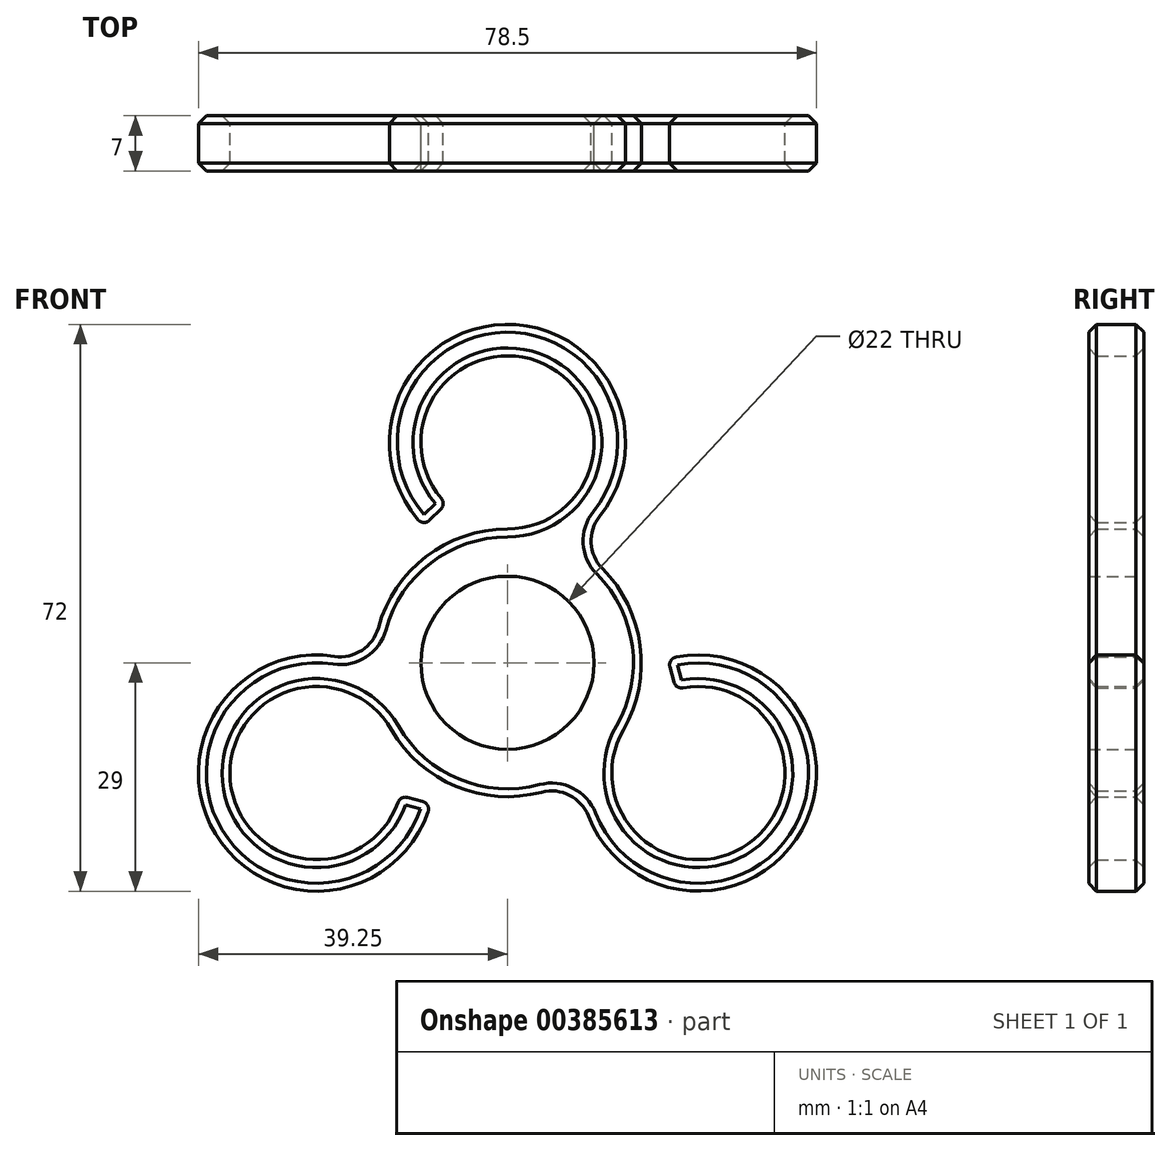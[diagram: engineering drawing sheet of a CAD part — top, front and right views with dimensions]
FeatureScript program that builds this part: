
annotation { "Feature Type Name" : "Feature", "Feature Type Description" : "" }
export const myFeature = defineFeature(function(context is Context, id is Id, definition is map)
    precondition{}
    {
        {
            var Q0;
            Q0=qCreatedBy(makeId("Front.planeOp"),FACE);
            var sketch = newSketch(context, id + "F0", { "sketchPlane" : qUnion([Q0])});
            skCircle(sketch, "E0", {"center": v(0, 0) * mm, "radius": 11 * mm});
            skArc(sketch, "E1", {"start": v(0, 17) * mm, "mid": v(-10.32, 13.5) * mm, "end": v(-16.4, 4.46) * mm});
            skArc(sketch, "E2", {"start": v(0, 17) * mm, "mid": v(4.63, 37.98) * mm, "end": v(-8.4, 20.9) * mm});
            skLineSegment(sketch, "E3", {"start": v(-8.46, 19.54) * mm, "end": v(-9.87, 18.13) * mm});
            skArc(sketch, "E4", {"start": v(11.7, 18.63) * mm, "mid": v(-0.3, 43) * mm, "end": v(-11.34, 18.18) * mm});
            skPoint(sketch, "E5.visualSharp", {"position": v(-7.78, 20.22) * mm});
            skArc(sketch, "E5.filletArc", {"start": v(-8.46, 19.54) * mm, "mid": v(-8.16, 20.2) * mm, "end": v(-8.4, 20.9) * mm});
            skPoint(sketch, "E6.visualSharp", {"position": v(-10.6, 17.4) * mm});
            skArc(sketch, "E6.filletArc", {"start": v(-11.34, 18.18) * mm, "mid": v(-10.62, 17.83) * mm, "end": v(-9.87, 18.13) * mm});
            skPoint(sketch, "E7.visualSharp", {"position": v(7.73, 15.14) * mm});
            skArc(sketch, "E7.filletArc", {"start": v(11.7, 18.63) * mm, "mid": v(10.62, 15.23) * mm, "end": v(12.06, 11.98) * mm});
            skPoint(sketch, "E8.1.0", {"position": v(-13.62, -16.85) * mm});
            skArc(sketch, "E8.1.1", {"start": v(-21.98, 0.83) * mm, "mid": v(-18.5, 1.58) * mm, "end": v(-16.4, 4.46) * mm});
            skArc(sketch, "E8.1.2", {"start": v(-21.98, 0.83) * mm, "mid": v(-37.1, -21.75) * mm, "end": v(-10.07, -18.9) * mm});
            skArc(sketch, "E8.1.3", {"start": v(-14.72, -8.5) * mm, "mid": v(-35.2, -14.98) * mm, "end": v(-13.9, -17.72) * mm});
            skPoint(sketch, "E8.1.4", {"position": v(-9.76, -17.88) * mm});
            skPoint(sketch, "E8.1.5", {"position": v(-16.98, -0.88) * mm});
            skLineSegment(sketch, "E8.1.6", {"start": v(-12.7, -17.1) * mm, "end": v(-10.76, -17.61) * mm});
            skArc(sketch, "E8.1.7", {"start": v(-10.07, -18.9) * mm, "mid": v(-10.14, -18.11) * mm, "end": v(-10.76, -17.61) * mm});
            skArc(sketch, "E8.1.8", {"start": v(-12.7, -17.1) * mm, "mid": v(-13.42, -17.17) * mm, "end": v(-13.9, -17.72) * mm});
            skPoint(sketch, "E8.2.0", {"position": v(21.4, -3.37) * mm});
            skArc(sketch, "E8.2.1", {"start": v(10.28, -19.45) * mm, "mid": v(7.88, -16.81) * mm, "end": v(4.34, -16.44) * mm});
            skArc(sketch, "E8.2.2", {"start": v(10.28, -19.45) * mm, "mid": v(37.38, -21.25) * mm, "end": v(21.41, 0.73) * mm});
            skArc(sketch, "E8.2.3", {"start": v(14.72, -8.5) * mm, "mid": v(30.58, -23) * mm, "end": v(22.3, -3.17) * mm});
            skPoint(sketch, "E8.2.4", {"position": v(20.37, 0.49) * mm});
            skPoint(sketch, "E8.2.5", {"position": v(9.25, -14.26) * mm});
            skLineSegment(sketch, "E8.2.6", {"start": v(21.15, -2.45) * mm, "end": v(20.63, -0.51) * mm});
            skArc(sketch, "E8.2.7", {"start": v(21.41, 0.73) * mm, "mid": v(20.75, 0.28) * mm, "end": v(20.63, -0.51) * mm});
            skArc(sketch, "E8.2.8", {"start": v(21.15, -2.45) * mm, "mid": v(21.58, -3.03) * mm, "end": v(22.3, -3.17) * mm});
            skArc(sketch, "E9.trimOffspring", {"start": v(-14.72, -8.5) * mm, "mid": v(-6.53, -15.7) * mm, "end": v(4.34, -16.44) * mm});
            skArc(sketch, "E10.trimOffspring", {"start": v(14.72, -8.5) * mm, "mid": v(16.86, 2.19) * mm, "end": v(12.06, 11.98) * mm});
            skSolve(sketch);
        }
        {
            var Q0;
            Q0=makeQuery(id+"F0.imprint","IMPRINT",FACE,{"disambiguationData":[TD([[makeQuery(id+"F0.imprint","IMPRINT",EDGE,{"derivedFrom":sQuery(id+"F0.wireOp",EDGE,"E0")}),-1.0]])]});
            extrude(context, id + "F1", {"entities" : qUnion([Q0]), "depth" : 7 * mm, "offsetDistance" : 25 * mm});
        }
        {
            var Q0;
            Q0=makeQuery(id+"F1.opExtrude","CAP_EDGE",EDGE,{"disambiguationData":[OSD([sQuery(id+"F0.wireOp",EDGE,"E10.trimOffspring")])],"isStart":false});
            var Q1;
            Q1=makeQuery(id+"F1.opExtrude","CAP_EDGE",EDGE,{"disambiguationData":[OSD([sQuery(id+"F0.wireOp",EDGE,"E10.trimOffspring")])],"isStart":true});
            chamfer(context, id + "F2", {"entities" : qUnion([Q0, Q1]), "width" : 1 * mm, "tangentPropagation" : true});
        }
    });
